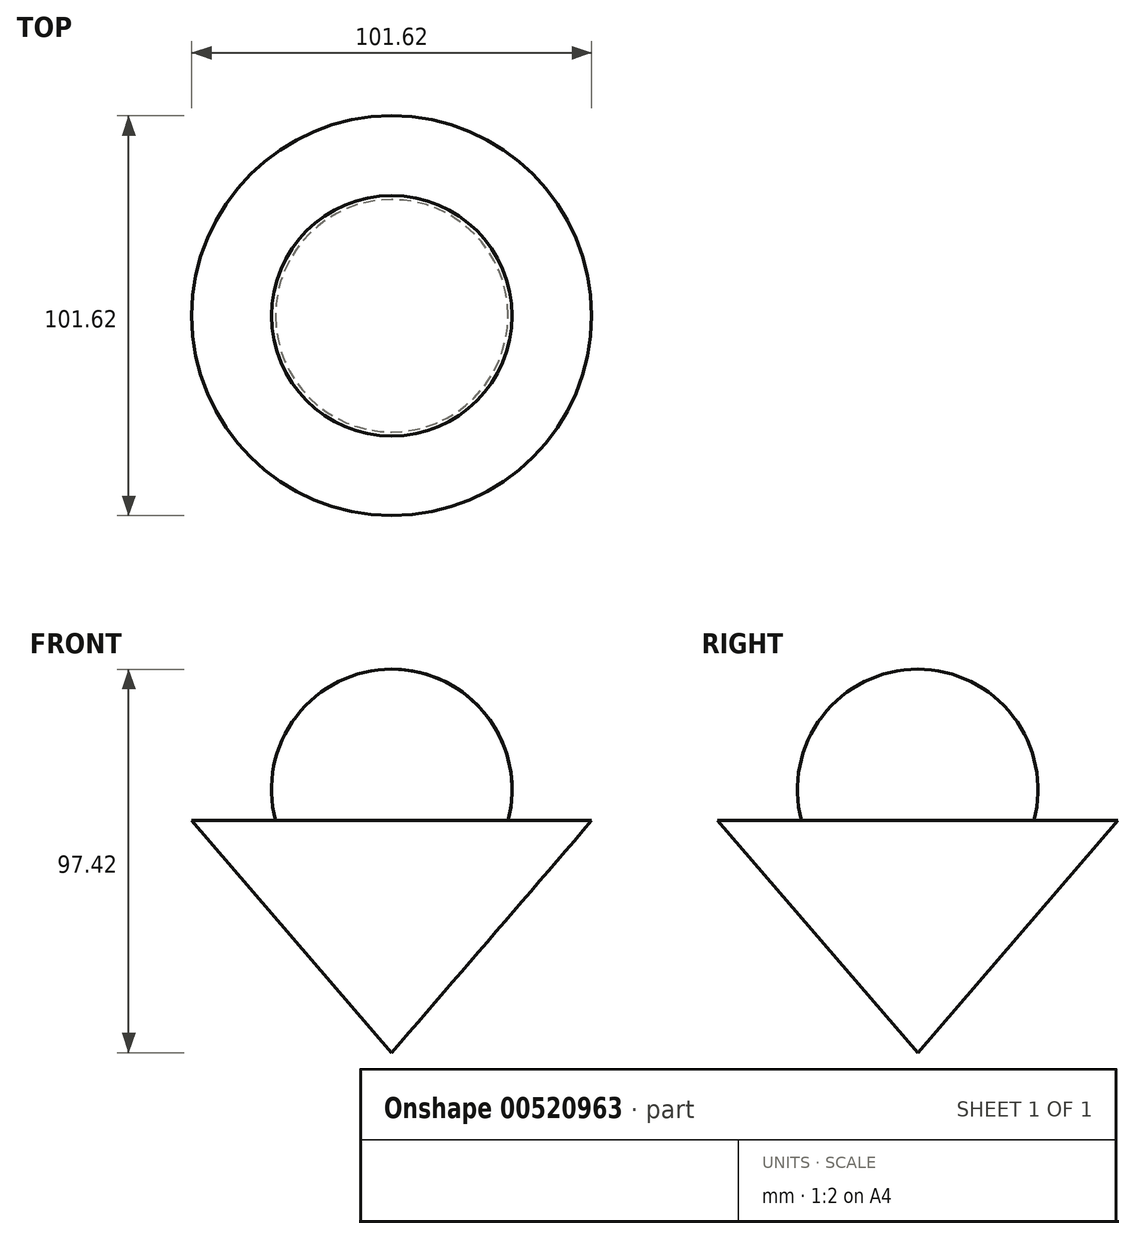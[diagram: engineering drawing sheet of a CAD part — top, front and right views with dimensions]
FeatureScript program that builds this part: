
annotation { "Feature Type Name" : "Feature", "Feature Type Description" : "" }
export const myFeature = defineFeature(function(context is Context, id is Id, definition is map)
    precondition{}
    {
        {
            var Q0;
            Q0=qCreatedBy(makeId("Front.planeOp"),FACE);
            var sketch = newSketch(context, id + "F0", { "sketchPlane" : qUnion([Q0])});
            skLineSegment(sketch, "E0.bottom", {"start": v(-49.93, 27.74) * mm, "end": v(46.43, 27.74) * mm});
            skLineSegment(sketch, "E0.top", {"start": v(-49.93, -31.24) * mm, "end": v(46.43, -31.24) * mm});
            skLineSegment(sketch, "E0.left", {"start": v(-49.93, 27.74) * mm, "end": v(-49.93, -31.24) * mm});
            skLineSegment(sketch, "E0.right", {"start": v(46.43, 27.74) * mm, "end": v(46.43, -31.24) * mm});
            skLineSegment(sketch, "E1", {"start": v(-49.93, 27.74) * mm, "end": v(-4.38, -31.24) * mm});
            skLineSegment(sketch, "E2", {"start": v(-4.38, -31.24) * mm, "end": v(46.43, 27.74) * mm});
            skLineSegment(sketch, "E3", {"start": v(-4.38, -31.24) * mm, "end": v(-4.38, 27.74) * mm});
            skCircle(sketch, "E4", {"center": v(-4.38, 35.62) * mm, "radius": 30.56 * mm});
            skLineSegment(sketch, "E5", {"start": v(-4.38, 27.74) * mm, "end": v(-4.38, 66.18) * mm});
            skSolve(sketch);
        }
        {
            var Q0;
            {var subQ0=sQuery(id+"F0.wireOp",EDGE,"E2");Q0=makeQuery(id+"F0.imprint","IMPRINT",FACE,{"disambiguationData":[TD([[makeQuery(id+"F0.imprint","IMPRINT",EDGE,{"derivedFrom":subQ0}),1.0]])]});}
            var Q1;
            {var subQ0=sQuery(id+"F0.wireOp",EDGE,"E3");var subQ1=sQuery(id+"F0.wireOp",EDGE,"E0.bottom");var subQ2=makeQuery(id+"F0.imprint","INTERSECT",VERTEX,{"derivedFrom":[subQ1,subQ0]});Q1=makeQuery(id+"F0.imprint","IMPRINT",FACE,{"disambiguationData":[TD([[makeQuery(id+"F0.imprint","IMPRINT",EDGE,{"disambiguationData":[TD([[subQ2,-1.0]])],"derivedFrom":subQ1}),-1.0]])]});}
            var Q2;
            {var subQ0=sQuery(id+"F0.wireOp",EDGE,"E0.bottom");var subQ1=makeQuery(id+"F0.imprint","INTERSECT",VERTEX,{"derivedFrom":[subQ0,sQuery(id+"F0.wireOp",EDGE,"E3")]});Q2=makeQuery(id+"F0.imprint","IMPRINT",FACE,{"disambiguationData":[TD([[makeQuery(id+"F0.imprint","IMPRINT",EDGE,{"disambiguationData":[TD([[subQ1,1.0]])],"derivedFrom":subQ0}),1.0]])]});}
            var Q3;
            Q3=sQuery(id+"F0.wireOp",EDGE,"E3");
            revolve(context, id + "F1", {"entities" : qUnion([Q0, Q1, Q2]), "axis" : qUnion([Q3]), "revolveType" : RevolveType.FULL});
        }
    });
